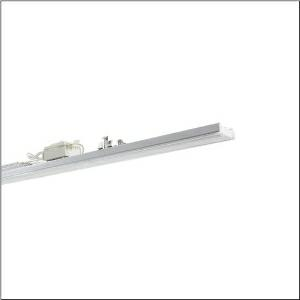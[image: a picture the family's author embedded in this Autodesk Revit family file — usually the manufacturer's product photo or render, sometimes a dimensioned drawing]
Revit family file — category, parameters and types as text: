
# Revit family: licross_r__21_recessed_mo_52te147n48xg_9933
name_source: partatom
category: Lighting Fixtures
units: mm (PartAtom-declared; Revit-internal decimal feet)

## family parameters
Cut with Voids When Loaded = No
Host = Face
Light Source = No
Part Type = Normal
Room Calculation Point = No
Round Connector Dimension = Use Diameter
Shared = No

## types (1)
- Licross® 21 Recessed MO (1 x LED, 8120 lm, 47.9 W, 4000K)
    Apparent Load = 48 VA
    CIE Flux Codes = 56 84 97 100 100
    Color Rendering = 80
    Color Temperature = 4000K
    Default Elevation = 1800 mm
    Description = Licross® 21 Recessed MO, luminaire insert, of sheet steel, galvanised, coil coated, white, length: 1.500mm, width: 66mm, height: 67mm, LED rated luminous flux: 8.120lm, light colour: 840, control gear: ON/OFF, with plug, 3-pole, with phase selection, mains connection: 220..240V, AC, 50/60Hz, rated input power: 48W, halogen-free wiring, primary light control with lens, of plastic, primary optical cover: cover, of PMMA, light emission: direct distribution, primary light characteristic: asymmetric, protection rating (complete): IP54, insulation class (complete): insulation class I (protective earthing), certification: CE, ENEC, VDE, UKCA, protection symbol: D if used in an environment with non-conductive dust loads with corresponding accessories, impact resistance: IK06, permissible ambient temperature for indoor applications: -35..+40°C, corresponds to IFS (International Featured Standards) requirements for safety and quality in the food industry, reducing of maximum allowable ambient temperature of 5°C with ceiling mounting, LABS conformity tested according to VDMA 24364:2018-05, packaging unit: 1 piece
    Height = 58 mm
    Lamp = 1 x LED
    Lamp Light Flux = 8120 lm
    Lamp Power = 47.9 W
    Lamp count = 1
    Length = 1500 mm
    Luminous efficacy = 170 lm/W
    Manufacturer = Siteco
    ModVariant = No
    Model = 52TE147N48XG
    Mounting Place = Ceiling
    Mounting Type = Pendant
    Number of Poles = 1
    OnlyDefault = Yes
    Power Factor = 1
    Product Name = Licross® 21 Recessed MO
    Product group = luminaire insert
    ProductGroupID = 902
    Protection Class = Protection class I
    Protection Degree = IP 54
    RLX_Detail_Level = 1
    RLX_Emergency_Light_Flux = 0 lm
    RLX_Emergency_Type = 0
    RLX_Emergency_Type_DB = No
    RlxData = <blob elided: 21353 chars, md5=0d717595>
    Socket = socket
    Standby Power = 0 W
    System Light Flux = 8120 lm
    System Power = 48 W
    Type Comments = Product without accessories
    Type Image = l_1296930.jpg
    URL = http://relux.com
    VarID = ---
    Voltage = 0 V
    Weight = 0.00 kg
    Width = 66 mm

## geometry (parser evidence)
native form markers: Blend x4, Sweep x9
no freeform markers — native parametric forms only
